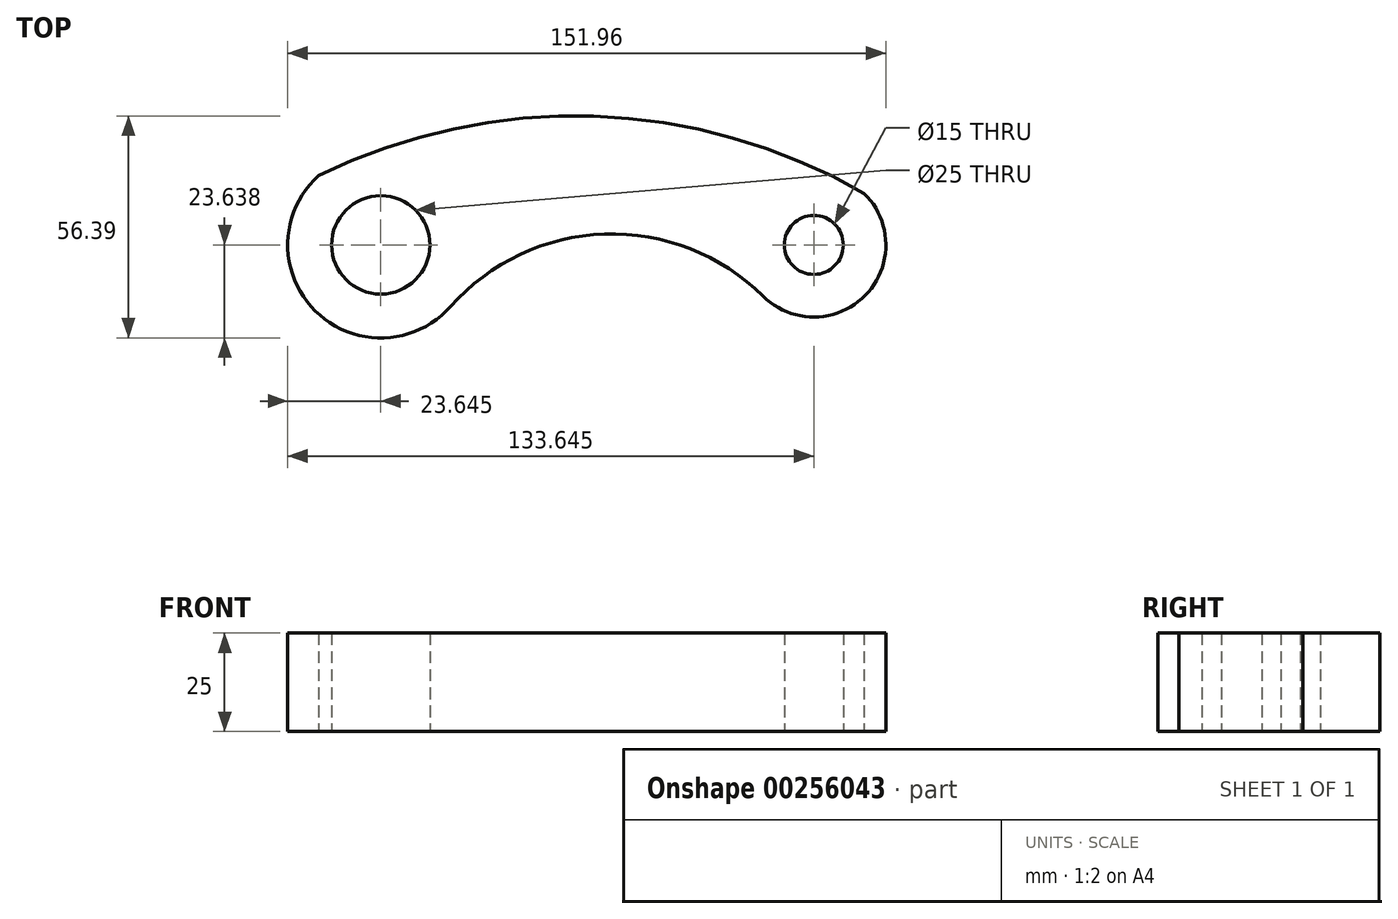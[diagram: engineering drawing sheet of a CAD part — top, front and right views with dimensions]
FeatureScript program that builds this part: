
annotation { "Feature Type Name" : "Feature", "Feature Type Description" : "" }
export const myFeature = defineFeature(function(context is Context, id is Id, definition is map)
    precondition{}
    {
        {
            var Q0;
            Q0=qCreatedBy(makeId("Top.planeOp"),FACE);
            var sketch = newSketch(context, id + "F0", { "sketchPlane" : qUnion([Q0])});
            skCircle(sketch, "E0", {"center": v(-105, 25.22) * mm, "radius": 6.25 * mm});
            skCircle(sketch, "E1", {"center": v(5, 25.22) * mm, "radius": 3.75 * mm});
            skCircle(sketch, "E2", {"center": v(5, 25.22) * mm, "radius": 7.5 * mm});
            skCircle(sketch, "E3", {"center": v(-105, 25.22) * mm, "radius": 12.5 * mm});
            skLineSegment(sketch, "E4", {"start": v(-105, 25.22) * mm, "end": v(-92.5, 25.22) * mm});
            skArc(sketch, "E5", {"start": v(-7.87, 12.2) * mm, "mid": v(-48.15, 27.97) * mm, "end": v(-87.29, 9.55) * mm});
            skArc(sketch, "E6", {"start": v(-120.82, 42.79) * mm, "mid": v(-121.64, 8.43) * mm, "end": v(-87.29, 9.55) * mm});
            skArc(sketch, "E7", {"start": v(-7.87, 12.2) * mm, "mid": v(18.07, 12.38) * mm, "end": v(17.8, 38.32) * mm});
            skArc(sketch, "E8", {"start": v(17.8, 38.32) * mm, "mid": v(-50.95, 57.9) * mm, "end": v(-120.82, 42.79) * mm});
            skSolve(sketch);
        }
        {
            var Q0;
            Q0=qCreatedBy(makeId("Top.planeOp"),FACE);
            var sketch = newSketch(context, id + "F1", { "sketchPlane" : qUnion([Q0])});
            skSolve(sketch);
        }
        {
            var Q0;
            Q0 = qSketchRegion(id + "F0", true);
            var Q1;
            Q1 = qSketchRegion(id + "F1", true);
            extrude(context, id + "F2", {"entities" : qUnion([Q0, Q1]), "depth" : 25 * mm});
        }
    });
